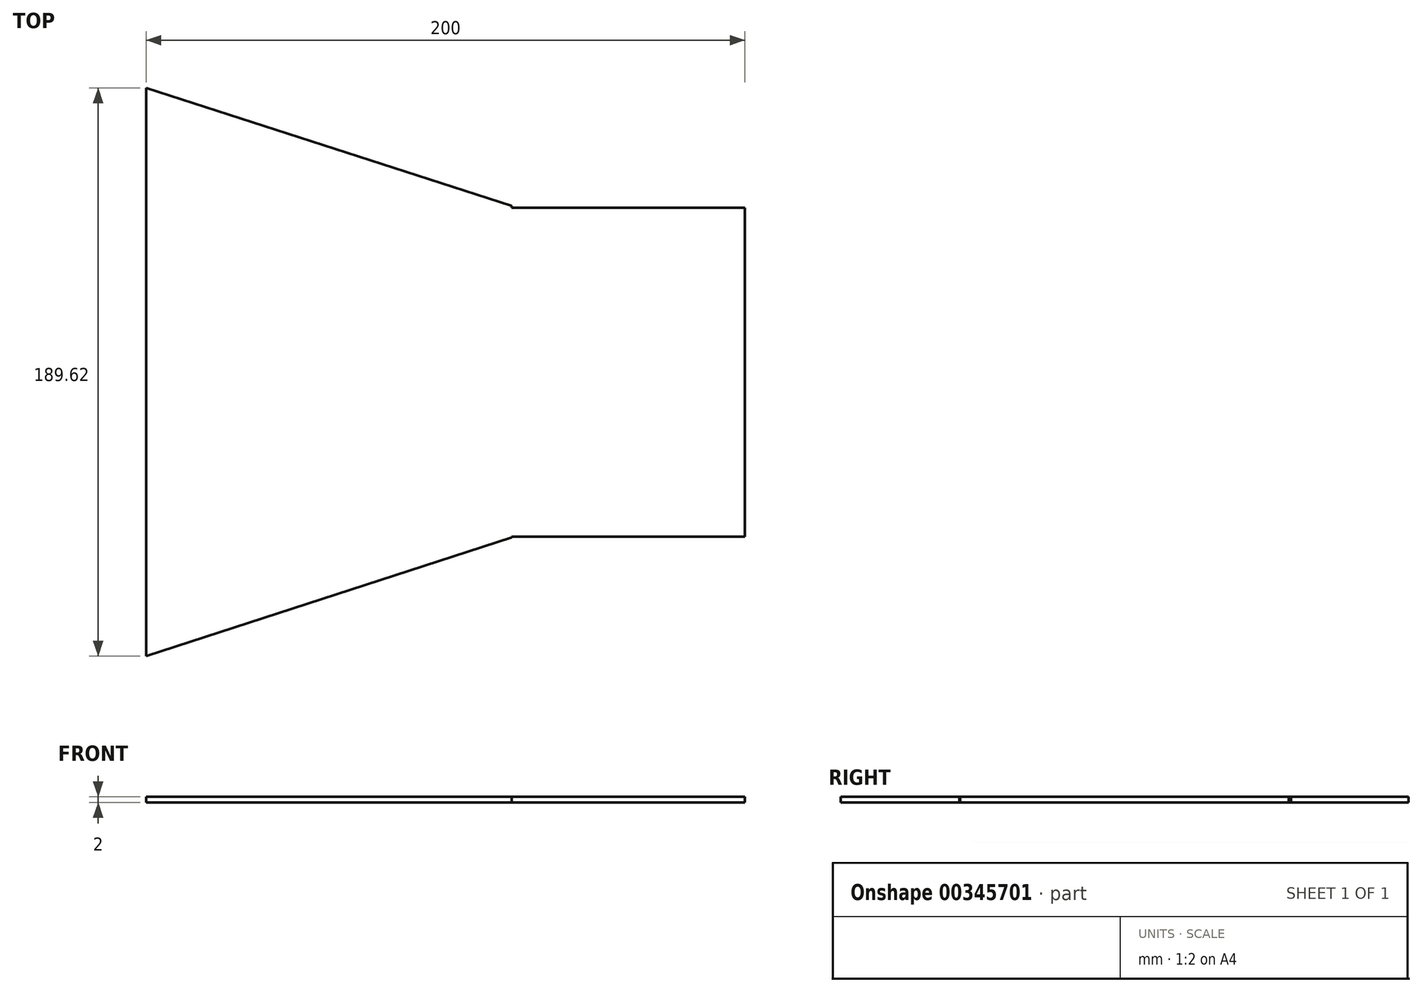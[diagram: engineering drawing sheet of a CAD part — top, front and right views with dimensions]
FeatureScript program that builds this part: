
annotation { "Feature Type Name" : "Feature", "Feature Type Description" : "" }
export const myFeature = defineFeature(function(context is Context, id is Id, definition is map)
    precondition{}
    {
        {
            var Q0;
            Q0=qCreatedBy(makeId("Top.planeOp"),FACE);
            var sketch = newSketch(context, id + "F0", { "sketchPlane" : qUnion([Q0])});
            skLineSegment(sketch, "E0.bottom", {"start": v(-739.73, 400) * mm, "end": v(739.73, 400) * mm});
            skLineSegment(sketch, "E0.top", {"start": v(-739.73, -400) * mm, "end": v(739.73, -400) * mm});
            skLineSegment(sketch, "E0.left", {"start": v(-739.73, 400) * mm, "end": v(-739.73, -400) * mm});
            skLineSegment(sketch, "E0.right", {"start": v(739.73, 400) * mm, "end": v(739.73, -400) * mm});
            skPoint(sketch, "E0.middle", {"position": v(0, 0) * mm});
            skLineSegment(sketch, "E1", {"start": v(-98.52, 54.84) * mm, "end": v(-98.52, 94.84) * mm});
            skLineSegment(sketch, "E2", {"start": v(-98.52, 94.84) * mm, "end": v(23.55, 55.56) * mm});
            skLineSegment(sketch, "E3", {"start": v(-98.52, -54.8) * mm, "end": v(-98.52, -94.78) * mm});
            skLineSegment(sketch, "E4", {"start": v(-98.52, -94.78) * mm, "end": v(23.55, -55.25) * mm});
            skLineSegment(sketch, "E5.bottom", {"start": v(-98.52, 54.84) * mm, "end": v(101.48, 54.84) * mm});
            skLineSegment(sketch, "E5.top", {"start": v(-98.52, -54.94) * mm, "end": v(101.48, -54.94) * mm});
            skLineSegment(sketch, "E5.left", {"start": v(-98.52, 54.84) * mm, "end": v(-98.52, -54.94) * mm});
            skLineSegment(sketch, "E5.right", {"start": v(101.48, 54.84) * mm, "end": v(101.48, -54.94) * mm});
            skLineSegment(sketch, "E6", {"start": v(23.55, 55.56) * mm, "end": v(23.55, -55.25) * mm});
            skSolve(sketch);
        }
        {
            var Q0;
            {var subQ0=sQuery(id+"F0.wireOp",EDGE,"E5.left");var subQ3=makeQuery(id+"F0.imprint","IMPRINT",VERTEX,{"derivedFrom":subQ0});Q0=makeQuery(id+"F0.imprint","IMPRINT",FACE,{"disambiguationData":[TD([[makeQuery(id+"F0.imprint","IMPRINT",EDGE,{"disambiguationData":[TD([[subQ3,1.0]])],"derivedFrom":subQ0}),1.0]])]});}
            var Q1;
            {var subQ0=sQuery(id+"F0.wireOp",EDGE,"E1");Q1=makeQuery(id+"F0.imprint","IMPRINT",FACE,{"disambiguationData":[TD([[makeQuery(id+"F0.imprint","IMPRINT",EDGE,{"derivedFrom":subQ0}),-1.0]])]});}
            var Q2;
            {var subQ0=sQuery(id+"F0.wireOp",EDGE,"E5.right");Q2=makeQuery(id+"F0.imprint","IMPRINT",FACE,{"disambiguationData":[TD([[makeQuery(id+"F0.imprint","IMPRINT",EDGE,{"derivedFrom":subQ0}),-1.0]])]});}
            var Q3;
            {var subQ0=sQuery(id+"F0.wireOp",EDGE,"E3");Q3=makeQuery(id+"F0.imprint","IMPRINT",FACE,{"disambiguationData":[TD([[makeQuery(id+"F0.imprint","IMPRINT",EDGE,{"derivedFrom":subQ0}),1.0]])]});}
            extrude(context, id + "F1", {"entities" : qUnion([Q0, Q1, Q2, Q3]), "depth" : 2 * mm});
        }
        {
            var Q0;
            Q0=makeQuery(id+"F1.opExtrude","CAP_FACE",FACE,{"disambiguationData":[OSD([sQuery(id+"F0.wireOp",EDGE,"E1"),sQuery(id+"F0.wireOp",EDGE,"E2"),sQuery(id+"F0.wireOp",EDGE,"E3"),sQuery(id+"F0.wireOp",EDGE,"E4"),sQuery(id+"F0.wireOp",EDGE,"E5.bottom"),sQuery(id+"F0.wireOp",EDGE,"E5.top"),sQuery(id+"F0.wireOp",EDGE,"E5.left"),sQuery(id+"F0.wireOp",EDGE,"E5.right"),sQuery(id+"F0.wireOp",EDGE,"E6")])],"isStart":false});
            var sketch = newSketch(context, id + "F2", { "sketchPlane" : qUnion([Q0])});
            skLineSegment(sketch, "E7", {"start": v(0, 0) * mm, "end": v(-98.52, 0) * mm});
            skLineSegment(sketch, "E8", {"start": v(23.55, 54.84) * mm, "end": v(-98.52, 54.84) * mm});
            skLineSegment(sketch, "E9", {"start": v(-98.52, 54.84) * mm, "end": v(-98.52, -54.94) * mm});
            skLineSegment(sketch, "E10", {"start": v(-98.52, -54.94) * mm, "end": v(23.55, -54.94) * mm});
            skLineSegment(sketch, "E11", {"start": v(0, 0) * mm, "end": v(194.25, 0) * mm});
            skLineSegment(sketch, "E12", {"start": v(194.25, 0) * mm, "end": v(194.25, 34.18) * mm});
            skLineSegment(sketch, "E13", {"start": v(194.25, 34.18) * mm, "end": v(101.48, 34.18) * mm});
            skLineSegment(sketch, "E14", {"start": v(101.48, 34.18) * mm, "end": v(194.25, 0) * mm});
            skLineSegment(sketch, "E15", {"start": v(194.25, -34.73) * mm, "end": v(101.48, -34.73) * mm});
            skLineSegment(sketch, "E16", {"start": v(101.48, -34.73) * mm, "end": v(194.25, 0) * mm});
            skLineSegment(sketch, "E17", {"start": v(194.25, -34.73) * mm, "end": v(194.25, 0) * mm});
            skSolve(sketch);
        }
    });
